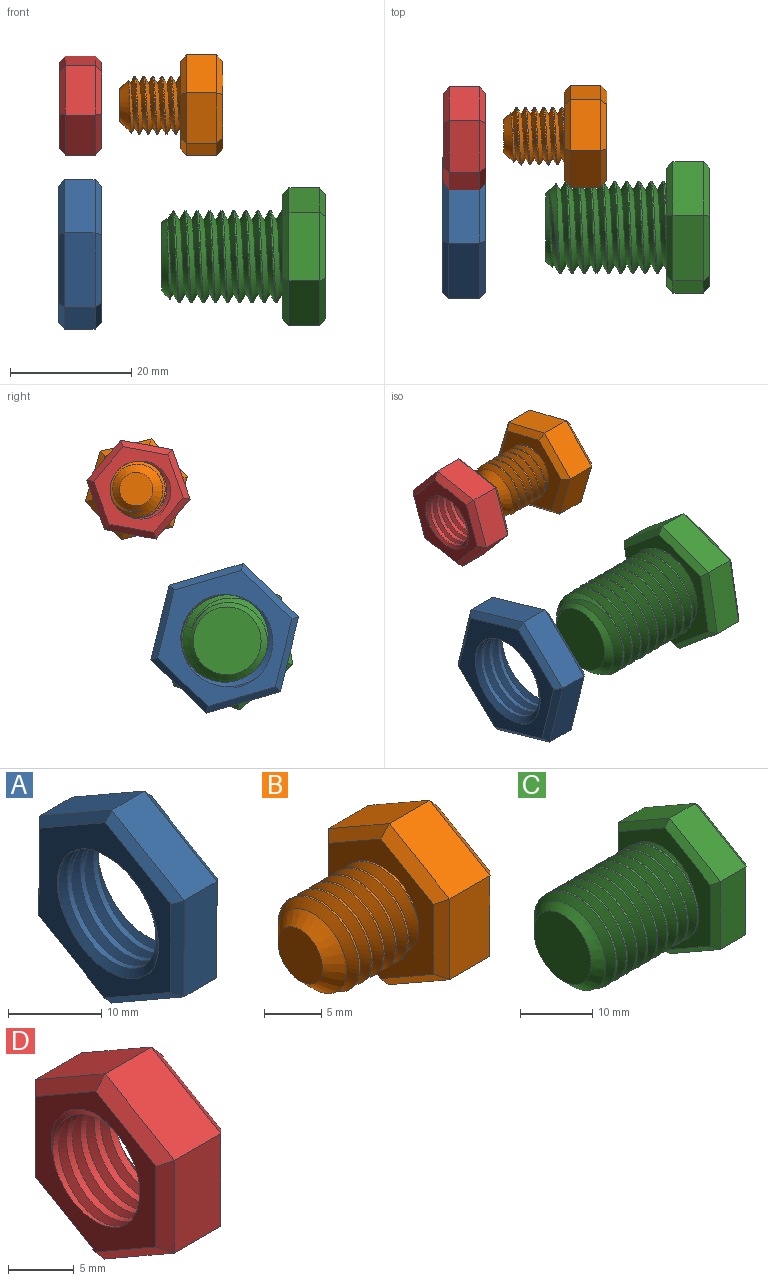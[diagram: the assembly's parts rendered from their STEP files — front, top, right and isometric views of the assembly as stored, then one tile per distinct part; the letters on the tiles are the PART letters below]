
ASSEMBLY  parts=4 mates=2
PART A: 23 faces, bbox 9.3x22.7x26 mm
  f0: cylinder r=7.24mm len=14.48mm, axis (1,0,0), area 111.6mm2, adj f7,f8,f21,f22
  f1: plane 10.98x6.38mm, normal (0,-0.5,0.86), area 63.5mm2, adj f2,f6,f14,f18
  f2: plane 12.7x5mm, normal (0,-1,0), area 63.5mm2, adj f1,f3,f12,f16
  f3: plane 11.02x6.32mm, normal (0,-0.5,-0.87), area 63.5mm2, adj f2,f4,f10,f15
  f4: plane 10.98x6.38mm, normal (0,0.5,-0.86), area 63.5mm2, adj f3,f5,f9,f17
  f5: plane 12.7x5mm, normal (0,1,0), area 63.5mm2, adj f4,f6,f11,f19
  f6: plane 11.02x6.32mm, normal (0,0.5,0.87), area 63.5mm2, adj f1,f5,f13,f20
  f7: plane 23.73x20.67mm, normal (-1,0,0), area 164.4mm2, adj f0,f9,f10,f11,f12,f13,f14,f21
  f8: plane 23.73x20.67mm, normal (1,0,0), area 164.4mm2, adj f0,f15,f16,f17,f18,f19,f20,f21
  f9: plane 10.99x6.96mm, normal (-0.71,0.36,-0.61), area 17.1mm2, adj f4,f7,f10,f11
  f10: plane 11.02x6.9mm, normal (-0.71,-0.35,-0.61), area 17.1mm2, adj f3,f7,f9,f12
  f11: plane 12.7x1.03mm, normal (-0.71,0.71,0), area 17.1mm2, adj f5,f7,f9,f13
  f12: plane 12.7x1.03mm, normal (-0.71,-0.71,0), area 17.1mm2, adj f2,f7,f10,f14
  f13: plane 11.02x6.9mm, normal (-0.71,0.35,0.61), area 17.1mm2, adj f6,f7,f11,f14
  f14: plane 10.99x6.96mm, normal (-0.71,-0.36,0.61), area 17.1mm2, adj f1,f7,f12,f13
  f15: plane 11.02x6.9mm, normal (0.71,-0.35,-0.61), area 17.1mm2, adj f3,f8,f16,f17
  f16: plane 12.7x1.03mm, normal (0.71,-0.71,0), area 17.1mm2, adj f2,f8,f15,f18
  f17: plane 10.99x6.96mm, normal (0.71,0.36,-0.61), area 17.1mm2, adj f4,f8,f15,f19
  f18: plane 10.99x6.96mm, normal (0.71,-0.36,0.61), area 17.1mm2, adj f1,f8,f16,f20
  f19: plane 12.7x1.03mm, normal (0.71,0.71,0), area 17.1mm2, adj f5,f8,f17,f20
  f20: plane 11.02x6.9mm, normal (0.71,0.35,0.61), area 17.1mm2, adj f6,f8,f18,f19
  f21: bspline ~19.31x16.73mm, area 223mm2, adj f0,f7,f8,f22
  f22: bspline ~19.31x16.73mm, area 223mm2, adj f0,f7,f8,f21
PART B: 25 faces, bbox 17.8x15.9x18.1 mm
  f0: cylinder r=4.75mm len=9.5mm, axis (1,0,0), area 28.1mm2, adj f1,f2,f4,f12
  f1: bspline ~10.97x9.91mm, area 196.7mm2, adj f0,f2,f4,f12
  f2: bspline ~10.97x10.66mm, area 196.6mm2, adj f0,f1,f4,f12
  f3: plane 5.5x5.5mm, normal (-1,0,0), area 23.8mm2, adj f4
  f4: cone r=4.75mm half-angle=45deg, axis (1,0,0), area 47.4mm2, adj f0,f1,f2,f3
  f5: plane 7.48x5mm, normal (0,-0.5,0.86), area 43.3mm2, adj f6,f10,f18,f22
  f6: plane 8.66x5mm, normal (0,-1,0), area 43.3mm2, adj f5,f7,f16,f20
  f7: plane 7.52x5mm, normal (0,-0.5,-0.87), area 43.3mm2, adj f6,f8,f14,f19
  f8: plane 7.48x5mm, normal (0,0.5,-0.86), area 43.3mm2, adj f7,f9,f13,f21
  f9: plane 8.66x5mm, normal (0,1,0), area 43.3mm2, adj f8,f10,f15,f23
  f10: plane 7.52x5mm, normal (0,0.5,0.87), area 43.3mm2, adj f5,f9,f17,f24
  f11: plane 15.01x13.03mm, normal (1,0,0), area 146.4mm2, adj f13,f14,f15,f16,f17,f18
  f12: plane 15.83x13.85mm, normal (-1,0,0), area 89.2mm2, adj f0,f1,f2,f19,f20,f21,f22,f23
  f13: plane 7.49x4.93mm, normal (0.71,0.36,-0.61), area 11.4mm2, adj f8,f11,f14,f15
  f14: plane 7.52x4.88mm, normal (0.71,-0.35,-0.61), area 11.4mm2, adj f7,f11,f13,f16
  f15: plane 8.66x1.03mm, normal (0.71,0.71,0), area 11.4mm2, adj f9,f11,f13,f17
  f16: plane 8.66x1.03mm, normal (0.71,-0.71,0), area 11.4mm2, adj f6,f11,f14,f18
  f17: plane 7.52x4.88mm, normal (0.71,0.35,0.61), area 11.4mm2, adj f10,f11,f15,f18
  f18: plane 7.49x4.93mm, normal (0.71,-0.36,0.61), area 11.4mm2, adj f5,f11,f16,f17
  f19: plane 7.52x4.88mm, normal (-0.71,-0.35,-0.61), area 11.4mm2, adj f7,f12,f20,f21
  f20: plane 8.66x1.03mm, normal (-0.71,-0.71,0), area 11.4mm2, adj f6,f12,f19,f22
  f21: plane 7.49x4.93mm, normal (-0.71,0.36,-0.61), area 11.4mm2, adj f8,f12,f19,f23
  f22: plane 7.49x4.93mm, normal (-0.71,-0.36,0.61), area 11.4mm2, adj f5,f12,f20,f24
  f23: plane 8.66x1.03mm, normal (-0.71,0.71,0), area 11.4mm2, adj f9,f12,f21,f24
  f24: plane 7.52x4.88mm, normal (-0.71,0.35,0.61), area 11.4mm2, adj f10,f12,f22,f23
PART C: 26 faces, bbox 27.7x20x23.1 mm
  f0: cylinder r=7.6mm len=18mm, axis (1,0,0), area 137.6mm2, adj f1,f2,f5,f13
  f1: bspline ~20.88x17.55mm, area 705.6mm2, adj f0,f2,f4,f5,f13
  f2: bspline ~21.88x17.55mm, area 706.8mm2, adj f0,f1,f4,f5,f13
  f3: plane 11.2x11.2mm, normal (-1,0,0), area 98.5mm2, adj f4
  f4: cone r=7.6mm half-angle=45deg, axis (1,0,0), area 62.4mm2, adj f1,f2,f3,f5
  f5: cone r=7.6mm half-angle=45deg, axis (1,0,0), area 13mm2, adj f0,f1,f2,f4
  f6: plane 9.98x5.81mm, normal (0,-0.5,0.86), area 57.7mm2, adj f7,f11,f19,f23
  f7: plane 11.55x5mm, normal (0,-1,0), area 57.7mm2, adj f6,f8,f17,f21
  f8: plane 10.02x5.74mm, normal (0,-0.5,-0.87), area 57.7mm2, adj f7,f9,f15,f20
  f9: plane 9.98x5.81mm, normal (0,0.5,-0.86), area 57.7mm2, adj f8,f10,f14,f22
  f10: plane 11.55x5mm, normal (0,1,0), area 57.7mm2, adj f9,f11,f16,f24
  f11: plane 10.02x5.74mm, normal (0,0.5,0.87), area 57.7mm2, adj f6,f10,f18,f25
  f12: plane 20.78x18.04mm, normal (1,0,0), area 280.6mm2, adj f14,f15,f16,f17,f18,f19
  f13: plane 20.78x18.04mm, normal (-1,0,0), area 128.7mm2, adj f0,f1,f2,f20,f21,f22,f23,f24
  f14: plane 9.98x6.38mm, normal (0.71,0.36,-0.61), area 15.5mm2, adj f9,f12,f15,f16
  f15: plane 10.02x6.32mm, normal (0.71,-0.35,-0.61), area 15.5mm2, adj f8,f12,f14,f17
  f16: plane 11.55x1.04mm, normal (0.71,0.71,0), area 15.5mm2, adj f10,f12,f14,f18
  f17: plane 11.55x1.04mm, normal (0.71,-0.71,0), area 15.5mm2, adj f7,f12,f15,f19
  f18: plane 10.02x6.32mm, normal (0.71,0.35,0.61), area 15.5mm2, adj f11,f12,f16,f19
  f19: plane 9.98x6.38mm, normal (0.71,-0.36,0.61), area 15.5mm2, adj f6,f12,f17,f18
  f20: plane 10.02x6.32mm, normal (-0.71,-0.35,-0.61), area 15.5mm2, adj f8,f13,f21,f22
  f21: plane 11.55x1.04mm, normal (-0.71,-0.71,0), area 15.5mm2, adj f7,f13,f20,f23
  f22: plane 9.98x6.38mm, normal (-0.71,0.36,-0.61), area 15.5mm2, adj f9,f13,f20,f24
  f23: plane 9.98x6.38mm, normal (-0.71,-0.36,0.61), area 15.5mm2, adj f6,f13,f21,f25
  f24: plane 11.55x1.04mm, normal (-0.71,0.71,0), area 15.5mm2, adj f10,f13,f22,f25
  f25: plane 10.02x6.32mm, normal (-0.71,0.35,0.61), area 15.5mm2, adj f11,f13,f23,f24
PART D: 23 faces, bbox 9.1x15.4x17.7 mm
  f0: plane 7.49x5mm, normal (0,-0.5,0.86), area 43.3mm2, adj f1,f5,f13,f17
  f1: plane 8.66x5mm, normal (0,-1,0), area 43.3mm2, adj f0,f2,f11,f15
  f2: plane 7.51x5mm, normal (0,-0.5,-0.87), area 43.3mm2, adj f1,f3,f9,f14
  f3: plane 7.49x5mm, normal (0,0.5,-0.86), area 43.3mm2, adj f2,f4,f8,f16
  f4: plane 8.66x5mm, normal (0,1,0), area 43.3mm2, adj f3,f5,f10,f18
  f5: plane 7.51x5mm, normal (0,0.5,0.87), area 43.3mm2, adj f0,f4,f12,f19
  f6: plane 15.37x13.38mm, normal (-1,0,0), area 71.4mm2, adj f8,f9,f10,f11,f12,f13,f20,f21
  f7: plane 15.37x13.38mm, normal (1,0,0), area 71.4mm2, adj f14,f15,f16,f17,f18,f19,f20,f21
  f8: plane 7.49x4.93mm, normal (-0.71,0.36,-0.61), area 11.4mm2, adj f3,f6,f9,f10
  f9: plane 7.51x4.89mm, normal (-0.71,-0.35,-0.61), area 11.4mm2, adj f2,f6,f8,f11
  f10: plane 8.66x1.02mm, normal (-0.71,0.71,0), area 11.4mm2, adj f4,f6,f8,f12
  f11: plane 8.66x1.02mm, normal (-0.71,-0.71,0), area 11.4mm2, adj f1,f6,f9,f13
  f12: plane 7.51x4.89mm, normal (-0.71,0.35,0.61), area 11.4mm2, adj f5,f6,f10,f13
  f13: plane 7.49x4.93mm, normal (-0.71,-0.36,0.61), area 11.4mm2, adj f0,f6,f11,f12
  f14: plane 7.51x4.89mm, normal (0.71,-0.35,-0.61), area 11.4mm2, adj f2,f7,f15,f16
  f15: plane 8.66x1.02mm, normal (0.71,-0.71,0), area 11.4mm2, adj f1,f7,f14,f17
  f16: plane 7.49x4.93mm, normal (0.71,0.36,-0.61), area 11.4mm2, adj f3,f7,f14,f18
  f17: plane 7.49x4.93mm, normal (0.71,-0.36,0.61), area 11.4mm2, adj f0,f7,f15,f19
  f18: plane 8.66x1.02mm, normal (0.71,0.71,0), area 11.4mm2, adj f4,f7,f16,f19
  f19: plane 7.51x4.89mm, normal (0.71,0.35,0.61), area 11.4mm2, adj f5,f7,f17,f18
  f20: cylinder r=4.66mm len=9.32mm, axis (1,0,0), area 85.4mm2, adj f6,f7,f21,f22
  f21: bspline ~12.5x10.82mm, area 128.4mm2, adj f6,f7,f20,f22
  f22: bspline ~12.5x10.82mm, area 128.5mm2, adj f6,f7,f20,f21
PLACE A rot(axis=(0,0.6,-0.8),180deg) t=(-55.27,-6.86,23.48)mm fixed
PLACE B rot(axis=(-1,0,0),43.8deg) t=(-31.66,7.73,48.08)mm
PLACE C rot(axis=(1,0,0),109.9deg) t=(-14.77,-7.25,23.06)mm
PLACE D rot(axis=(1,0,0),100.2deg) t=(-48.16,7.38,48.02)mm fixed
MATE cylindrical C.f0 <-> A.f7  axis (-1,0,0) through (-38.27,-7.25,23.06)mm
MATE cylindrical B.f0 <-> D.f6  axis (-1,0,0) through (-45.16,7.73,48.08)mm
